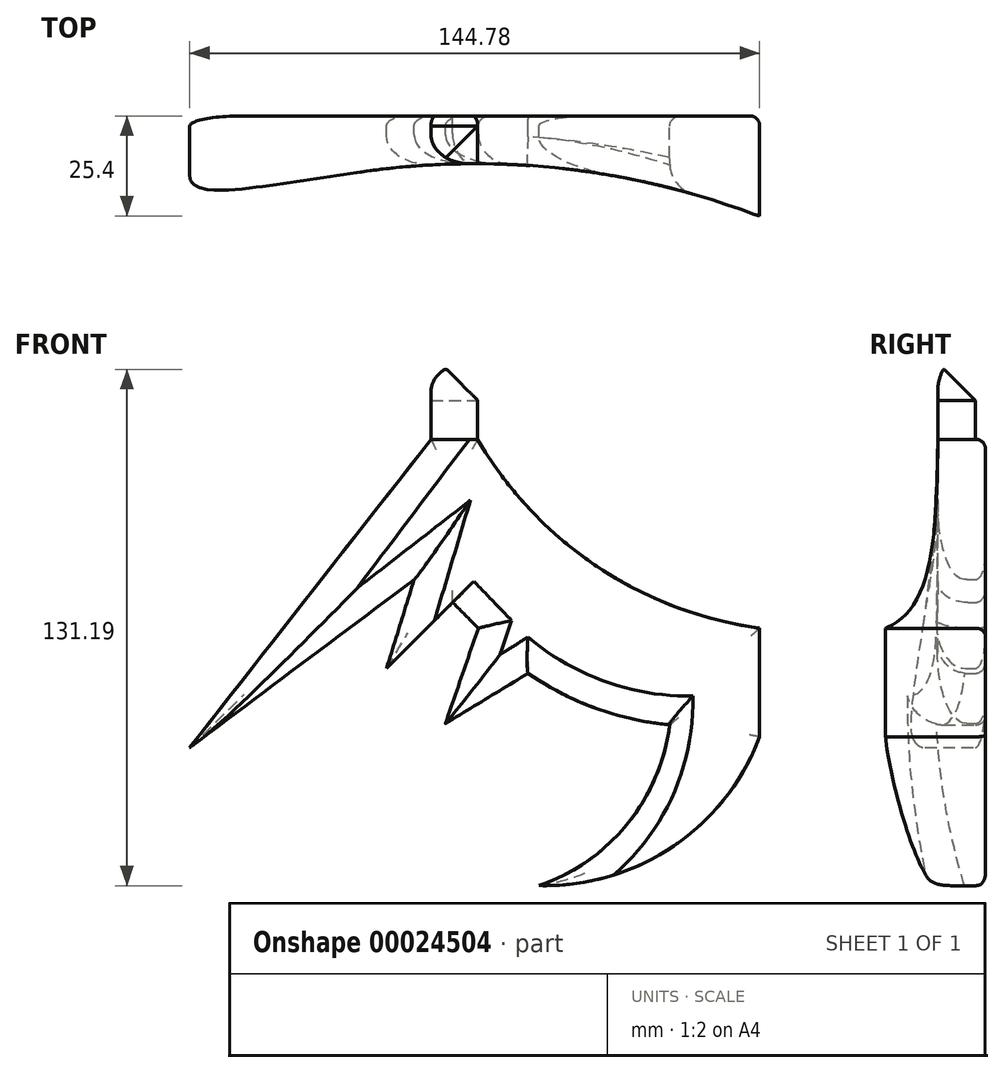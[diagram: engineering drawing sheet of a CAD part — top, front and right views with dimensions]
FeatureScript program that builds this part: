
annotation { "Feature Type Name" : "Feature", "Feature Type Description" : "" }
export const myFeature = defineFeature(function(context is Context, id is Id, definition is map)
    precondition{}
    {
        {
            var Q0;
            Q0=qCreatedBy(makeId("Front.planeOp"),FACE);
            var sketch = newSketch(context, id + "F0", { "sketchPlane" : qUnion([Q0])});
            skArc(sketch, "E0", {"start": v(-71.63, 48) * mm, "mid": v(-41.36, 15.73) * mm, "end": v(0, 0) * mm});
            skLineSegment(sketch, "E1", {"start": v(-71.63, 48) * mm, "end": v(-83.52, 48) * mm});
            skLineSegment(sketch, "E2", {"start": v(-83.52, 48) * mm, "end": v(-144.78, -30.33) * mm});
            skLineSegment(sketch, "E3", {"start": v(-144.78, -30.33) * mm, "end": v(-87.78, 12.34) * mm});
            skLineSegment(sketch, "E4", {"start": v(-87.78, 12.34) * mm, "end": v(-94.8, -10.21) * mm});
            skLineSegment(sketch, "E5", {"start": v(-94.8, -10.21) * mm, "end": v(-78.03, 6.55) * mm});
            skLineSegment(sketch, "E6", {"start": v(-78.03, 6.55) * mm, "end": v(-71.48, 0) * mm});
            skLineSegment(sketch, "E7", {"start": v(-71.48, 0) * mm, "end": v(-79.86, -24.23) * mm});
            skLineSegment(sketch, "E8", {"start": v(-79.86, -24.23) * mm, "end": v(-58.83, -11.43) * mm});
            skArc(sketch, "E9", {"start": v(-58.83, -11.43) * mm, "mid": v(-41.7, -20.31) * mm, "end": v(-22.86, -24.54) * mm});
            skArc(sketch, "E10", {"start": v(-56.08, -65.38) * mm, "mid": v(-33.62, -49.72) * mm, "end": v(-22.86, -24.54) * mm});
            skArc(sketch, "E11", {"start": v(-56.08, -65.38) * mm, "mid": v(-22.02, -55.42) * mm, "end": v(0, -27.58) * mm});
            skLineSegment(sketch, "E12", {"start": v(0, -27.58) * mm, "end": v(0, 2.9) * mm});
            skSolve(sketch);
        }
        {
            var Q0;
            Q0 = qSketchRegion(id + "F0", true);
            extrude(context, id + "F1", {"entities" : qUnion([Q0]), "depth" : 25.4 * mm});
        }
        {
            var Q0;
            Q0=qCreatedBy(makeId("Top.planeOp"),FACE);
            var sketch = newSketch(context, id + "F2", { "sketchPlane" : qUnion([Q0])});
            skLineSegment(sketch, "E13", {"start": v(-145.59, -25.93) * mm, "end": v(-93.35, -51.36) * mm});
            skLineSegment(sketch, "E14", {"start": v(-93.35, -51.36) * mm, "end": v(0, -25.54) * mm});
            skArc(sketch, "E15", {"start": v(0, -25.54) * mm, "mid": v(-72.83, -12.16) * mm, "end": v(-145.59, -25.93) * mm});
            skSolve(sketch);
        }
        {
            var Q0;
            Q0 = qSketchRegion(id + "F2", true);
            extrude(context, id + "F3", {"entities" : qUnion([Q0]), "operationType" : NewBodyOperationType.REMOVE, "oppositeDirection" : true, "depth" : 104.33 * mm, "hasSecondDirection" : true, "secondDirectionOppositeDirection" : false, "secondDirectionDepth" : 79.89 * mm});
        }
        {
            var Q0;
            Q0=makeQuery(id+"F3.boolean.opBoolean","INTERSECT",EDGE,{"derivedFrom":[makeQuery(id+"F1.opExtrude","SWEPT_FACE",FACE,{"disambiguationData":[OSD([sQuery(id+"F0.wireOp",EDGE,"E2")])]}),makeQuery(id+"F3.opExtrude","SWEPT_FACE",FACE,{"disambiguationData":[OSD([sQuery(id+"F2.wireOp",EDGE,"E15")])]})]});
            var Q1;
            Q1=makeQuery(id+"F3.boolean.opBoolean","INTERSECT",EDGE,{"derivedFrom":[makeQuery(id+"F1.opExtrude","SWEPT_FACE",FACE,{"disambiguationData":[OSD([sQuery(id+"F0.wireOp",EDGE,"E4")])]}),makeQuery(id+"F3.opExtrude","SWEPT_FACE",FACE,{"disambiguationData":[OSD([sQuery(id+"F2.wireOp",EDGE,"E15")])]})]});
            var Q2;
            Q2=makeQuery(id+"F3.boolean.opBoolean","INTERSECT",EDGE,{"derivedFrom":[makeQuery(id+"F1.opExtrude","SWEPT_FACE",FACE,{"disambiguationData":[OSD([sQuery(id+"F0.wireOp",EDGE,"E6")])]}),makeQuery(id+"F3.opExtrude","SWEPT_FACE",FACE,{"disambiguationData":[OSD([sQuery(id+"F2.wireOp",EDGE,"E15")])]})]});
            var Q3;
            Q3=makeQuery(id+"F3.boolean.opBoolean","INTERSECT",EDGE,{"derivedFrom":[makeQuery(id+"F1.opExtrude","SWEPT_FACE",FACE,{"disambiguationData":[OSD([sQuery(id+"F0.wireOp",EDGE,"E3")])]}),makeQuery(id+"F3.opExtrude","SWEPT_FACE",FACE,{"disambiguationData":[OSD([sQuery(id+"F2.wireOp",EDGE,"E15")])]})]});
            var Q4;
            Q4=makeQuery(id+"F3.boolean.opBoolean","INTERSECT",EDGE,{"derivedFrom":[makeQuery(id+"F1.opExtrude","SWEPT_FACE",FACE,{"disambiguationData":[OSD([sQuery(id+"F0.wireOp",EDGE,"E7")])]}),makeQuery(id+"F3.opExtrude","SWEPT_FACE",FACE,{"disambiguationData":[OSD([sQuery(id+"F2.wireOp",EDGE,"E15")])]})]});
            var Q5;
            Q5=makeQuery(id+"F3.boolean.opBoolean","INTERSECT",EDGE,{"derivedFrom":[makeQuery(id+"F1.opExtrude","SWEPT_FACE",FACE,{"disambiguationData":[OSD([sQuery(id+"F0.wireOp",EDGE,"E9")])]}),makeQuery(id+"F3.opExtrude","SWEPT_FACE",FACE,{"disambiguationData":[OSD([sQuery(id+"F2.wireOp",EDGE,"E15")])]})]});
            var Q6;
            Q6=makeQuery(id+"F3.boolean.opBoolean","INTERSECT",EDGE,{"derivedFrom":[makeQuery(id+"F1.opExtrude","SWEPT_FACE",FACE,{"disambiguationData":[OSD([sQuery(id+"F0.wireOp",EDGE,"E10")])]}),makeQuery(id+"F3.opExtrude","SWEPT_FACE",FACE,{"disambiguationData":[OSD([sQuery(id+"F2.wireOp",EDGE,"E15")])]})]});
            var Q7;
            Q7=makeQuery(id+"F3.boolean.opBoolean","INTERSECT",EDGE,{"derivedFrom":[makeQuery(id+"F1.opExtrude","SWEPT_FACE",FACE,{"disambiguationData":[OSD([sQuery(id+"F0.wireOp",EDGE,"E8")])]}),makeQuery(id+"F3.opExtrude","SWEPT_FACE",FACE,{"disambiguationData":[OSD([sQuery(id+"F2.wireOp",EDGE,"E15")])]})]});
            var Q8;
            Q8=makeQuery(id+"F3.boolean.opBoolean","INTERSECT",EDGE,{"disambiguationData":[OD(0.0)],"derivedFrom":[makeQuery(id+"F1.opExtrude","CAP_FACE",FACE,{"disambiguationData":[OSD([sQuery(id+"F0.wireOp",EDGE,"E0"),sQuery(id+"F0.wireOp",EDGE,"E1"),sQuery(id+"F0.wireOp",EDGE,"E2"),sQuery(id+"F0.wireOp",EDGE,"E3"),sQuery(id+"F0.wireOp",EDGE,"E4"),sQuery(id+"F0.wireOp",EDGE,"E5"),sQuery(id+"F0.wireOp",EDGE,"E6"),sQuery(id+"F0.wireOp",EDGE,"E7"),sQuery(id+"F0.wireOp",EDGE,"E8"),sQuery(id+"F0.wireOp",EDGE,"E9"),sQuery(id+"F0.wireOp",EDGE,"E10"),sQuery(id+"F0.wireOp",EDGE,"E11"),sQuery(id+"F0.wireOp",EDGE,"E12")])],"isStart":false}),makeQuery(id+"F3.opExtrude","SWEPT_FACE",FACE,{"disambiguationData":[OSD([sQuery(id+"F2.wireOp",EDGE,"E15")])]})]});
            fillet(context, id + "F4", {"entities" : qUnion([Q0, Q1, Q2, Q3, Q4, Q5, Q6, Q7, Q8]), "radius" : 7.62 * mm, "tangentPropagation" : true, "allowEdgeOverflow" : false});
        }
        {
            var Q0;
            Q0=makeQuery(id+"F1.opExtrude","CAP_FACE",FACE,{"disambiguationData":[OSD([sQuery(id+"F0.wireOp",EDGE,"E0"),sQuery(id+"F0.wireOp",EDGE,"E1"),sQuery(id+"F0.wireOp",EDGE,"E2"),sQuery(id+"F0.wireOp",EDGE,"E3"),sQuery(id+"F0.wireOp",EDGE,"E4"),sQuery(id+"F0.wireOp",EDGE,"E5"),sQuery(id+"F0.wireOp",EDGE,"E6"),sQuery(id+"F0.wireOp",EDGE,"E7"),sQuery(id+"F0.wireOp",EDGE,"E8"),sQuery(id+"F0.wireOp",EDGE,"E9"),sQuery(id+"F0.wireOp",EDGE,"E10"),sQuery(id+"F0.wireOp",EDGE,"E11"),sQuery(id+"F0.wireOp",EDGE,"E12")])],"isStart":true});
            fillet(context, id + "F5", {"entities" : qUnion([Q0]), "radius" : 2.54 * mm, "tangentPropagation" : true, "allowEdgeOverflow" : false});
        }
        {
            var Q0;
            Q0=qCreatedBy(makeId("Front.planeOp"),FACE);
            cPlane(context, id + "F6", {"entities" : qUnion([Q0]), "cplaneType" : CPlaneType.OFFSET, "offset" : 7.62 * mm, "width" : 152.4 * mm, "height" : 152.4 * mm});
        }
        {
            var Q0;
            Q0=makeQuery(id+"F1.opExtrude","SWEPT_FACE",FACE,{"disambiguationData":[OSD([sQuery(id+"F0.wireOp",EDGE,"E1")])]});
            extrude(context, id + "F7", {"entities" : qUnion([Q0]), "depth" : 17.78 * mm});
        }
        {
            var Q0;
            Q0=makeQuery(id+"F7.opExtrude","CAP_EDGE",EDGE,{"disambiguationData":[OSD([sQuery(id+"F0.wireOp",EDGE,"E0"),sQuery(id+"F0.wireOp",EDGE,"E1")])],"isStart":false});
            var Q1;
            Q1=makeQuery(id+"F7.opExtrude","CAP_EDGE",EDGE,{"disambiguationData":[OSD([sQuery(id+"F0.wireOp",EDGE,"E1")])],"isStart":false});
            chamfer(context, id + "F8", {"entities" : qUnion([Q0, Q1]), "width" : 7.87 * mm, "tangentPropagation" : true});
        }
    });
